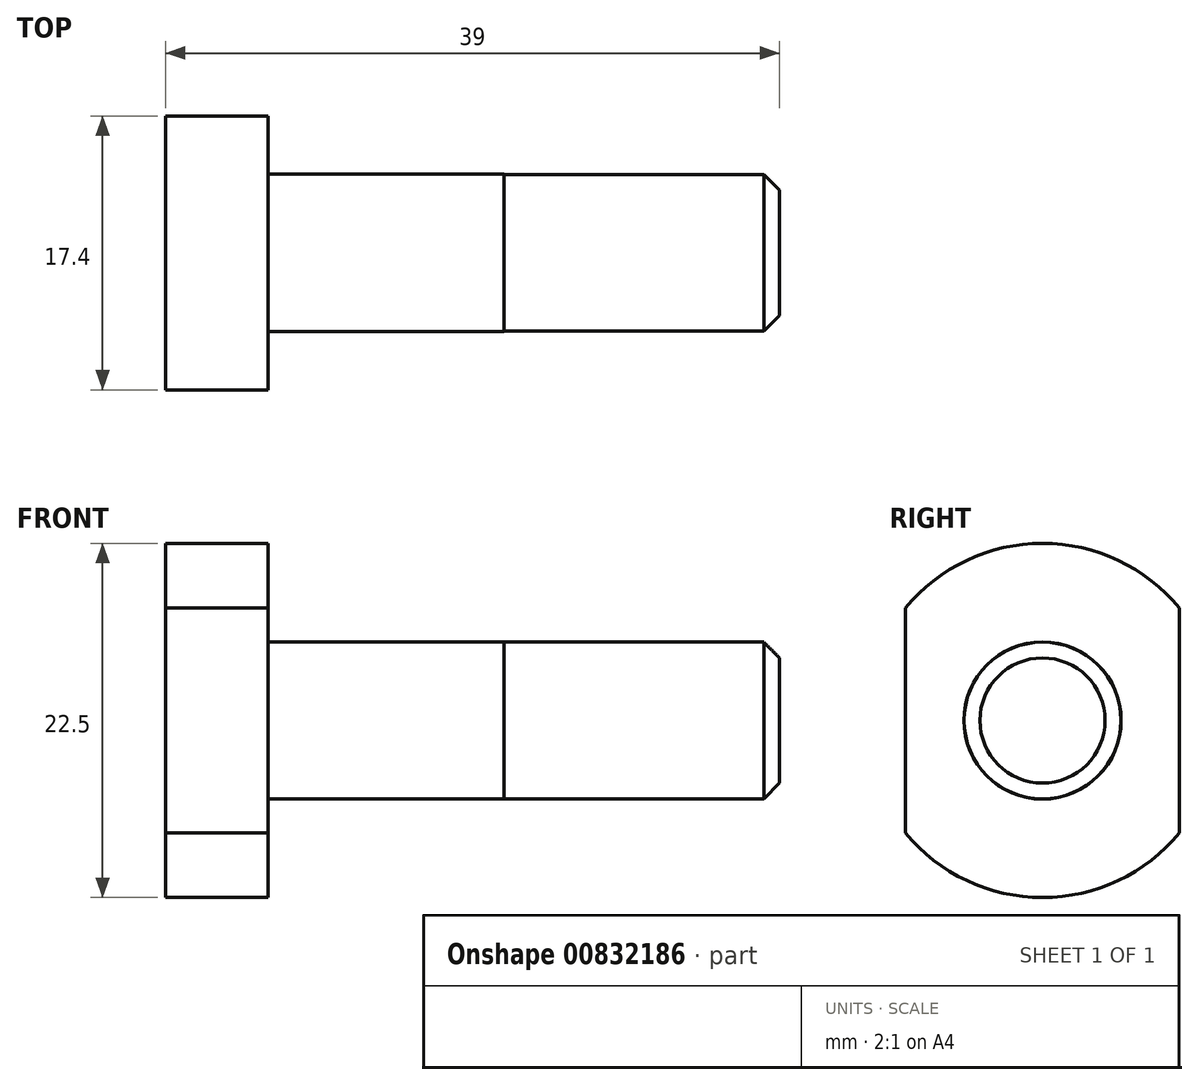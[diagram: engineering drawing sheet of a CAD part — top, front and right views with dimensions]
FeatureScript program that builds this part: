
annotation { "Feature Type Name" : "Feature", "Feature Type Description" : "" }
export const myFeature = defineFeature(function(context is Context, id is Id, definition is map)
    precondition{}
    {
        {
            var Q0;
            Q0=qCreatedBy(makeId("Front.planeOp"),FACE);
            var sketch = newSketch(context, id + "F0", { "sketchPlane" : qUnion([Q0])});
            skLineSegment(sketch, "E0", {"start": v(0, 0) * mm, "end": v(39, 0) * mm});
            skLineSegment(sketch, "E1", {"start": v(39, 0) * mm, "end": v(39, 4.98) * mm});
            skLineSegment(sketch, "E2", {"start": v(39, 4.98) * mm, "end": v(21.5, 4.98) * mm});
            skLineSegment(sketch, "E3", {"start": v(6.5, 5) * mm, "end": v(6.5, 11.25) * mm});
            skLineSegment(sketch, "E4", {"start": v(6.5, 11.25) * mm, "end": v(0, 11.25) * mm});
            skLineSegment(sketch, "E5", {"start": v(0, 11.25) * mm, "end": v(0, 0) * mm});
            skLineSegment(sketch, "E6", {"start": v(6.5, 5) * mm, "end": v(21.5, 5) * mm});
            skLineSegment(sketch, "E7", {"start": v(21.5, 4.98) * mm, "end": v(21.5, 5) * mm});
            skSolve(sketch);
        }
        {
            var Q0;
            Q0=makeQuery(id+"F0.imprint","IMPRINT",FACE,{"disambiguationData":[TD([[makeQuery(id+"F0.imprint","IMPRINT",EDGE,{"derivedFrom":sQuery(id+"F0.wireOp",EDGE,"E0")}),1.0]])]});
            var Q1;
            Q1 = qSketchRegion(id + "F0", true);
            var Q2;
            Q2=makeQuery(id+"F0.imprint","IMPRINT",FACE,{"disambiguationData":[TD([[makeQuery(id+"F0.imprint","IMPRINT",EDGE,{"derivedFrom":sQuery(id+"F0.wireOp",EDGE,"E0")}),1.0]])]});
            var Q3;
            Q3=makeQuery(id+"F0.imprint","IMPRINT",FACE,{"disambiguationData":[TD([[makeQuery(id+"F0.imprint","IMPRINT",EDGE,{"derivedFrom":sQuery(id+"F0.wireOp",EDGE,"E0")}),1.0]])]});
            var Q4;
            Q4=sQuery(id+"F0.wireOp",EDGE,"E0");
            revolve(context, id + "F1", {"surfaceOperationType" : NewSurfaceOperationType.NEW, "entities" : qUnion([Q0, Q1, Q2, Q3]), "axis" : qUnion([Q4]), "revolveType" : RevolveType.FULL});
        }
        {
            var Q0;
            Q0=makeQuery(id+"F1.opRevolve","SWEPT_FACE",FACE,{"disambiguationData":[OSD([sQuery(id+"F0.wireOp",EDGE,"E5")])]});
            var sketch = newSketch(context, id + "F2", { "sketchPlane" : qUnion([Q0])});
            skLineSegment(sketch, "E8.bottom", {"start": v(-8.7, 7.13) * mm, "end": v(-11.25, 7.13) * mm});
            skLineSegment(sketch, "E8.top", {"start": v(-8.7, -7.13) * mm, "end": v(-11.25, -7.13) * mm});
            skLineSegment(sketch, "E8.left", {"start": v(-8.7, 7.13) * mm, "end": v(-8.7, -7.13) * mm});
            skLineSegment(sketch, "E8.right", {"start": v(-11.25, 7.13) * mm, "end": v(-11.25, -7.13) * mm});
            skLineSegment(sketch, "E9.bottom", {"start": v(8.7, 7.13) * mm, "end": v(11.25, 7.13) * mm});
            skLineSegment(sketch, "E9.top", {"start": v(8.7, -7.13) * mm, "end": v(11.25, -7.13) * mm});
            skLineSegment(sketch, "E9.left", {"start": v(8.7, 7.13) * mm, "end": v(8.7, -7.13) * mm});
            skLineSegment(sketch, "E9.right", {"start": v(11.25, 7.13) * mm, "end": v(11.25, -7.13) * mm});
            skSolve(sketch);
        }
        {
            var Q0;
            Q0 = qSketchRegion(id + "F2", true);
            var Q1;
            Q1=makeQuery(id+"F1.opRevolve","SWEPT_FACE",FACE,{"disambiguationData":[OSD([sQuery(id+"F0.wireOp",EDGE,"E3")])]});
            extrude(context, id + "F3", {"entities" : qUnion([Q0]), "operationType" : NewBodyOperationType.REMOVE, "endBound" : BoundingType.UP_TO_SURFACE, "oppositeDirection" : true, "depth" : 25 * mm, "endBoundEntityFace" : qUnion([Q1]), "offsetDistance" : 25 * mm});
        }
        {
            var Q0;
            Q0=makeQuery(id+"F1.opRevolve","SWEPT_EDGE",EDGE,{"disambiguationData":[OSD([sQuery(id+"F0.wireOp",EDGE,"E1"),sQuery(id+"F0.wireOp",EDGE,"E2")])]});
            chamfer(context, id + "F4", {"entities" : qUnion([Q0]), "width" : 1 * mm, "tangentPropagation" : true});
        }
    });
